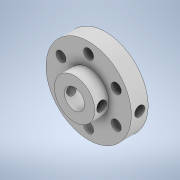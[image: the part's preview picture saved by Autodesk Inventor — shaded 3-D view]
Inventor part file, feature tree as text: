
AUTODESK INVENTOR PART (.ipt)
format: ipt  version: 2020.3 (Build 243373000, 373)  size: 204,800 bytes
history: native  units: mm
features: thread x10, extrude x6, sketch x6, pattern_circular x1, plane x1
ambient origin geometry x8: Origin, YZ Plane, XZ Plane, XY Plane, X Axis, Y Axis, Z Axis, Center Point
bodies: Solid1 (feature_tree)
feature tree (24):
  extrude  "Extrusion1"  Depth=5.0mm TaperAngle=0.0deg
  extrude  "Extrusion2"  Depth=6.0mm
  extrude  "Extrusion3"  Depth=19.0mm
  pattern_circular  "Circular Pattern1"  Count=6 Angle=360.0deg
  extrude  "Extrusion4"  Depth=10.0mm
  plane  "Work Plane1"
  extrude  "Extrusion5"  Depth=10.0mm TaperAngle=0.0deg
  extrude  "Extrusion6"  Depth=10.0mm
  thread  "Thread1"  [1 undecoded]
  thread  "Thread2"  [1 undecoded]
  thread  "Thread3"  [1 undecoded]
  thread  "Thread4"  [1 undecoded]
  thread  "Thread5"  [1 undecoded]
  thread  "Thread6"  [1 undecoded]
  thread  "Thread7"  [1 undecoded]
  thread  "Thread8"  [1 undecoded]
  thread  "Thread9"  [1 undecoded]
  thread  "Thread10"  [1 undecoded]
  sketch  "Sketch1"  dims[d0=25.4mm d1=5.0mm d2=0.0mm]
  sketch  "Sketch2"  dims[d3=12.0mm d4=6.0mm]
  sketch  "Sketch3"  dims[d5=4.2mm d6=0.0mm d7=19.0mm]
  sketch  "Sketch4"  dims[d8=3.0mm]
  sketch  "Sketch6"  dims[d9=5.0mm d10=0.0mm d11=60.0mm d12=360.0deg]
  sketch  "Sketch7"  dims[d14=19.0mm d15=3.0mm d16=10.0mm d17=0.0mm d18=12.7mm d19=2.5mm d20=3.0mm d21=25.4mm d22=0.0mm d23=3.0mm d24=2.1mm d25=25.4mm d26=0.0mm d27=10.222mm d28=0.0mm d29=5.0mm d30=0.0mm d31=5.0mm d32=0.0mm d33=5.0mm d34=0.0mm d35=5.0mm d36=0.0mm d37=5.0mm d38=0.0mm d39=3.402mm d40=0.0mm d41=3.402mm d42=0.0mm d43=5.0mm d44=0.0mm d45=10.222mm d46=0.0mm]
note: 10 required parameter values undecoded (feature->parameter linkage not recoverable at this tier; creation-order binding heuristic only, values carry confidence <= 0.55)
